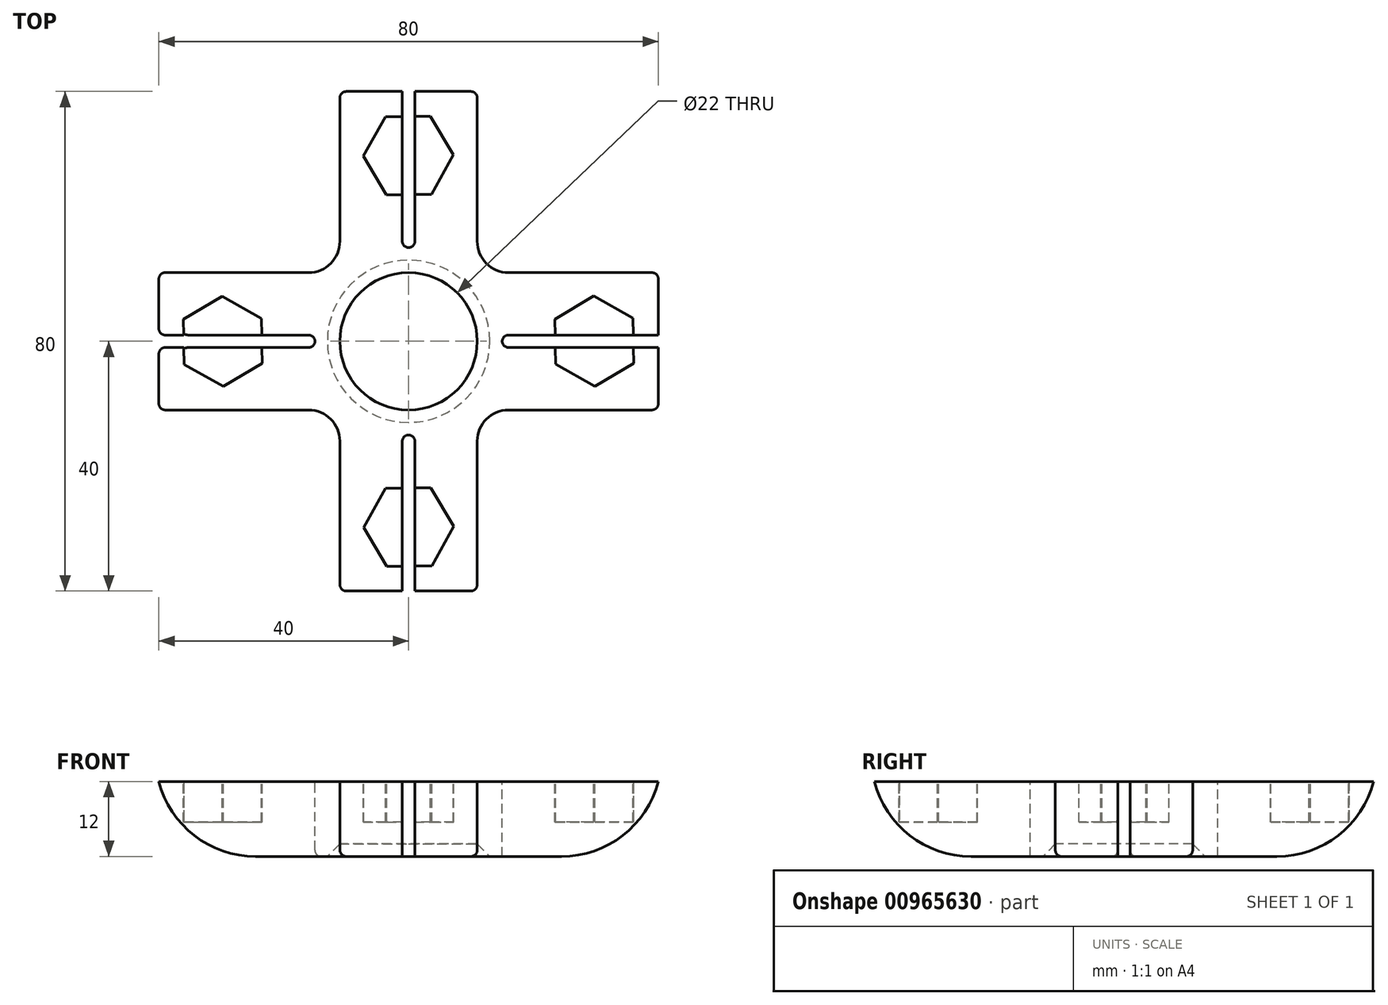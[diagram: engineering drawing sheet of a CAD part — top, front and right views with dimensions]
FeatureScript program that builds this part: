
annotation { "Feature Type Name" : "Feature", "Feature Type Description" : "" }
export const myFeature = defineFeature(function(context is Context, id is Id, definition is map)
    precondition{}
    {
        {
            var Q0;
            Q0=qCreatedBy(makeId("Front.planeOp"),FACE);
            var sketch = newSketch(context, id + "F0", { "sketchPlane" : qUnion([Q0])});
            skLineSegment(sketch, "E0.bottom", {"start": v(-11, 0) * mm, "end": v(11, 0) * mm});
            skLineSegment(sketch, "E0.top", {"start": v(-11, -40) * mm, "end": v(-1, -40) * mm});
            skLineSegment(sketch, "E0.left", {"start": v(-11, -16) * mm, "end": v(-11, -40) * mm});
            skLineSegment(sketch, "E0.right", {"start": v(11, -16) * mm, "end": v(11, -40) * mm});
            skLineSegment(sketch, "E1.1.0", {"start": v(40, -11) * mm, "end": v(40, -1) * mm});
            skLineSegment(sketch, "E1.1.2", {"start": v(16, 11) * mm, "end": v(40, 11) * mm});
            skLineSegment(sketch, "E1.2.0", {"start": v(11, 40) * mm, "end": v(1, 40) * mm});
            skLineSegment(sketch, "E1.3.0", {"start": v(-40, 11) * mm, "end": v(-40, 1) * mm});
            skLineSegment(sketch, "E1.3.1", {"start": v(-16, 11) * mm, "end": v(-40, 11) * mm});
            skLineSegment(sketch, "E1.3.2", {"start": v(-16, -11) * mm, "end": v(-40, -11) * mm});
            skPoint(sketch, "E1.center", {"position": v(0, 0) * mm});
            skPoint(sketch, "E2.orphan", {"position": v(0, 11) * mm});
            skLineSegment(sketch, "E3.trimOffspring", {"start": v(-11, 16) * mm, "end": v(-11, 40) * mm});
            skLineSegment(sketch, "E4.trimOffspring", {"start": v(11, 16) * mm, "end": v(11, 40) * mm});
            skLineSegment(sketch, "E5.trimOffspring", {"start": v(16, -11) * mm, "end": v(40, -11) * mm});
            skPoint(sketch, "E6.orphan", {"position": v(0, -11) * mm});
            skPoint(sketch, "E7.visualSharp", {"position": v(-40, 11) * mm});
            skLineSegment(sketch, "E7.filletArc", {"start": v(-40, 11) * mm, "end": v(-40, 11) * mm});
            skPoint(sketch, "E8.visualSharp", {"position": v(-40, -11) * mm});
            skLineSegment(sketch, "E8.filletArc", {"start": v(-40, -11) * mm, "end": v(-40, -11) * mm});
            skPoint(sketch, "E9.visualSharp", {"position": v(-11, -40) * mm});
            skLineSegment(sketch, "E9.filletArc", {"start": v(-11, -40) * mm, "end": v(-11, -40) * mm});
            skPoint(sketch, "E10.visualSharp", {"position": v(11, -40) * mm});
            skLineSegment(sketch, "E10.filletArc", {"start": v(11, -40) * mm, "end": v(11, -40) * mm});
            skPoint(sketch, "E11.visualSharp", {"position": v(40, -11) * mm});
            skLineSegment(sketch, "E11.filletArc", {"start": v(40, -11) * mm, "end": v(40, -11) * mm});
            skPoint(sketch, "E12.visualSharp", {"position": v(40, 11) * mm});
            skLineSegment(sketch, "E12.filletArc", {"start": v(40, 11) * mm, "end": v(40, 11) * mm});
            skPoint(sketch, "E13.visualSharp", {"position": v(11, 40) * mm});
            skLineSegment(sketch, "E13.filletArc", {"start": v(11, 40) * mm, "end": v(11, 40) * mm});
            skPoint(sketch, "E14.visualSharp", {"position": v(-11, 40) * mm});
            skLineSegment(sketch, "E14.filletArc", {"start": v(-11, 40) * mm, "end": v(-11, 40) * mm});
            skArc(sketch, "E15.filletArc", {"start": v(-16, 11) * mm, "mid": v(-12.46, 12.46) * mm, "end": v(-11, 16) * mm});
            skArc(sketch, "E16.filletArc", {"start": v(11, 16) * mm, "mid": v(12.46, 12.46) * mm, "end": v(16, 11) * mm});
            skArc(sketch, "E17.filletArc", {"start": v(16, -11) * mm, "mid": v(12.46, -12.46) * mm, "end": v(11, -16) * mm});
            skArc(sketch, "E18.filletArc", {"start": v(-11, -16) * mm, "mid": v(-12.46, -12.46) * mm, "end": v(-16, -11) * mm});
            skLineSegment(sketch, "E19.0", {"start": v(-1, 40) * mm, "end": v(-1, 16) * mm});
            skLineSegment(sketch, "E20.0", {"start": v(1, 40) * mm, "end": v(1, 16) * mm});
            skLineSegment(sketch, "E21", {"start": v(0, 11) * mm, "end": v(0, 11) * mm});
            skLineSegment(sketch, "E22.trimOffspring", {"start": v(-1, 40) * mm, "end": v(-11, 40) * mm});
            skLineSegment(sketch, "E23.1.0", {"start": v(-40, -1) * mm, "end": v(-16, -1) * mm});
            skPoint(sketch, "E23.1.1", {"position": v(-11, 0) * mm});
            skLineSegment(sketch, "E23.1.2", {"start": v(-40, 1) * mm, "end": v(-16, 1) * mm});
            skLineSegment(sketch, "E23.1.3", {"start": v(-11, 0) * mm, "end": v(-11, 0) * mm});
            skLineSegment(sketch, "E23.2.0", {"start": v(1, -40) * mm, "end": v(1, -16) * mm});
            skLineSegment(sketch, "E23.2.2", {"start": v(-1, -40) * mm, "end": v(-1, -16) * mm});
            skLineSegment(sketch, "E23.2.3", {"start": v(0, -11) * mm, "end": v(0, -11) * mm});
            skLineSegment(sketch, "E23.3.0", {"start": v(40, 1) * mm, "end": v(16, 1) * mm});
            skPoint(sketch, "E23.3.1", {"position": v(11, 0) * mm});
            skLineSegment(sketch, "E23.3.2", {"start": v(40, -1) * mm, "end": v(16, -1) * mm});
            skLineSegment(sketch, "E23.3.3", {"start": v(11, 0) * mm, "end": v(11, 0) * mm});
            skLineSegment(sketch, "E24.trimOffspring", {"start": v(40, 1) * mm, "end": v(40, 11) * mm});
            skLineSegment(sketch, "E25.trimOffspring", {"start": v(1, -40) * mm, "end": v(11, -40) * mm});
            skLineSegment(sketch, "E26.trimOffspring", {"start": v(-40, -1) * mm, "end": v(-40, -11) * mm});
            skPoint(sketch, "E27.visualSharp", {"position": v(-11, -1) * mm});
            skPoint(sketch, "E28.visualSharp", {"position": v(-11, 1) * mm});
            skArc(sketch, "E28.filletArc", {"start": v(-15, 0) * mm, "mid": v(-15.3, 0.7) * mm, "end": v(-16, 1) * mm});
            skArc(sketch, "E29.filletArc", {"start": v(-16, -1) * mm, "mid": v(-15.3, -0.7) * mm, "end": v(-15, 0) * mm});
            skPoint(sketch, "E30.visualSharp", {"position": v(1, 11) * mm});
            skArc(sketch, "E30.filletArc", {"start": v(0, 15) * mm, "mid": v(0.7, 15.3) * mm, "end": v(1, 16) * mm});
            skPoint(sketch, "E31.visualSharp", {"position": v(-1, 11) * mm});
            skArc(sketch, "E31.filletArc", {"start": v(-1, 16) * mm, "mid": v(-0.7, 15.3) * mm, "end": v(0, 15) * mm});
            skPoint(sketch, "E32.visualSharp", {"position": v(11, 1) * mm});
            skArc(sketch, "E32.filletArc", {"start": v(16, 1) * mm, "mid": v(15.3, 0.7) * mm, "end": v(15, 0) * mm});
            skPoint(sketch, "E33.visualSharp", {"position": v(11, -1) * mm});
            skArc(sketch, "E33.filletArc", {"start": v(15, 0) * mm, "mid": v(15.3, -0.7) * mm, "end": v(16, -1) * mm});
            skPoint(sketch, "E34.visualSharp", {"position": v(-1, -11) * mm});
            skArc(sketch, "E34.filletArc", {"start": v(0, -15) * mm, "mid": v(-0.7, -15.3) * mm, "end": v(-1, -16) * mm});
            skPoint(sketch, "E35.visualSharp", {"position": v(1, -11) * mm});
            skArc(sketch, "E35.filletArc", {"start": v(1, -16) * mm, "mid": v(0.7, -15.3) * mm, "end": v(0, -15) * mm});
            skSolve(sketch);
        }
        {
            var Q0;
            Q0=qCreatedBy(makeId("Front.planeOp"),FACE);
            var sketch = newSketch(context, id + "F1", { "sketchPlane" : qUnion([Q0])});
            skCircle(sketch, "E36.cCircle", {"center": v(-0.02, -29.75) * mm, "radius": 6.25 * mm, "construction": true});
            skLineSegment(sketch, "E36.0", {"start": v(3.5, -36.05) * mm, "end": v(-3.71, -35.95) * mm});
            skLineSegment(sketch, "E36.1", {"start": v(-3.71, -35.95) * mm, "end": v(-7.24, -29.65) * mm});
            skLineSegment(sketch, "E36.2", {"start": v(-7.24, -29.65) * mm, "end": v(-3.54, -23.45) * mm});
            skLineSegment(sketch, "E36.3", {"start": v(-3.54, -23.45) * mm, "end": v(3.67, -23.55) * mm});
            skLineSegment(sketch, "E36.4", {"start": v(3.67, -23.55) * mm, "end": v(7.2, -29.85) * mm});
            skLineSegment(sketch, "E36.5", {"start": v(7.2, -29.85) * mm, "end": v(3.5, -36.05) * mm});
            skPoint(sketch, "E36.0.midPoint", {"position": v(-0.1, -36) * mm});
            skCircle(sketch, "E37.1.0", {"center": v(29.75, -0.02) * mm, "radius": 6.25 * mm, "construction": true});
            skPoint(sketch, "E37.1.1", {"position": v(36, -0.1) * mm});
            skLineSegment(sketch, "E37.1.2", {"start": v(23.55, 3.67) * mm, "end": v(29.85, 7.2) * mm});
            skLineSegment(sketch, "E37.1.3", {"start": v(35.95, -3.71) * mm, "end": v(29.65, -7.24) * mm});
            skLineSegment(sketch, "E37.1.4", {"start": v(29.85, 7.2) * mm, "end": v(36.05, 3.5) * mm});
            skLineSegment(sketch, "E37.1.5", {"start": v(23.45, -3.54) * mm, "end": v(23.55, 3.67) * mm});
            skLineSegment(sketch, "E37.1.6", {"start": v(29.65, -7.24) * mm, "end": v(23.45, -3.54) * mm});
            skLineSegment(sketch, "E37.1.7", {"start": v(36.05, 3.5) * mm, "end": v(35.95, -3.71) * mm});
            skCircle(sketch, "E37.2.0", {"center": v(0.02, 29.75) * mm, "radius": 6.25 * mm, "construction": true});
            skPoint(sketch, "E37.2.1", {"position": v(0.1, 36) * mm});
            skLineSegment(sketch, "E37.2.2", {"start": v(-3.67, 23.55) * mm, "end": v(-7.2, 29.85) * mm});
            skLineSegment(sketch, "E37.2.3", {"start": v(3.71, 35.95) * mm, "end": v(7.24, 29.65) * mm});
            skLineSegment(sketch, "E37.2.4", {"start": v(-7.2, 29.85) * mm, "end": v(-3.5, 36.05) * mm});
            skLineSegment(sketch, "E37.2.5", {"start": v(3.54, 23.45) * mm, "end": v(-3.67, 23.55) * mm});
            skLineSegment(sketch, "E37.2.6", {"start": v(7.24, 29.65) * mm, "end": v(3.54, 23.45) * mm});
            skLineSegment(sketch, "E37.2.7", {"start": v(-3.5, 36.05) * mm, "end": v(3.71, 35.95) * mm});
            skCircle(sketch, "E37.3.0", {"center": v(-29.75, 0.02) * mm, "radius": 6.25 * mm, "construction": true});
            skPoint(sketch, "E37.3.1", {"position": v(-36, 0.1) * mm});
            skLineSegment(sketch, "E37.3.2", {"start": v(-23.55, -3.67) * mm, "end": v(-29.85, -7.2) * mm});
            skLineSegment(sketch, "E37.3.3", {"start": v(-35.95, 3.71) * mm, "end": v(-29.65, 7.24) * mm});
            skLineSegment(sketch, "E37.3.4", {"start": v(-29.85, -7.2) * mm, "end": v(-36.05, -3.5) * mm});
            skLineSegment(sketch, "E37.3.5", {"start": v(-23.45, 3.54) * mm, "end": v(-23.55, -3.67) * mm});
            skLineSegment(sketch, "E37.3.6", {"start": v(-29.65, 7.24) * mm, "end": v(-23.45, 3.54) * mm});
            skLineSegment(sketch, "E37.3.7", {"start": v(-36.05, -3.5) * mm, "end": v(-35.95, 3.71) * mm});
            skPoint(sketch, "E37.center", {"position": v(0, 0) * mm});
            skSolve(sketch);
        }
        {
            var Q0;
            Q0=qCreatedBy(makeId("Front.planeOp"),FACE);
            var sketch = newSketch(context, id + "F2", { "sketchPlane" : qUnion([Q0])});
            skCircle(sketch, "E38", {"center": v(0, 0) * mm, "radius": 11 * mm});
            skSolve(sketch);
        }
        {
            var Q0;
            Q0 = qSketchRegion(id + "F0", true);
            extrude(context, id + "F3", {"entities" : qUnion([Q0]), "depth" : 12 * mm, "offsetDistance" : 25 * mm});
        }
        {
            var Q0;
            Q0 = qSketchRegion(id + "F1", true);
            extrude(context, id + "F4", {"entities" : qUnion([Q0]), "depth" : 6.5 * mm, "offsetDistance" : 25 * mm});
        }
        {
            var Q0;
            Q0 = qSketchRegion(id + "F2", true);
            extrude(context, id + "F5", {"entities" : qUnion([Q0]), "depth" : 25 * mm, "offsetDistance" : 25 * mm});
        }
        {
            var Q0;
            Q0=makeQuery(id+"F5.opExtrude","SWEPT_BODY",BODY,{"disambiguationData":[OSD([sQuery(id+"F2.wireOp",EDGE,"E38")])]});
            var Q1;
            Q1=makeQuery(id+"F4.opExtrude","SWEPT_BODY",BODY,{"disambiguationData":[OSD([sQuery(id+"F1.wireOp",EDGE,"E37.1.2"),sQuery(id+"F1.wireOp",EDGE,"E37.1.3"),sQuery(id+"F1.wireOp",EDGE,"E37.1.4"),sQuery(id+"F1.wireOp",EDGE,"E37.1.5"),sQuery(id+"F1.wireOp",EDGE,"E37.1.6"),sQuery(id+"F1.wireOp",EDGE,"E37.1.7")])]});
            var Q2;
            Q2=makeQuery(id+"F4.opExtrude","SWEPT_BODY",BODY,{"disambiguationData":[OSD([sQuery(id+"F1.wireOp",EDGE,"E37.2.2"),sQuery(id+"F1.wireOp",EDGE,"E37.2.3"),sQuery(id+"F1.wireOp",EDGE,"E37.2.4"),sQuery(id+"F1.wireOp",EDGE,"E37.2.5"),sQuery(id+"F1.wireOp",EDGE,"E37.2.6"),sQuery(id+"F1.wireOp",EDGE,"E37.2.7")])]});
            var Q3;
            Q3=makeQuery(id+"F4.opExtrude","SWEPT_BODY",BODY,{"disambiguationData":[OSD([sQuery(id+"F1.wireOp",EDGE,"E37.3.2"),sQuery(id+"F1.wireOp",EDGE,"E37.3.3"),sQuery(id+"F1.wireOp",EDGE,"E37.3.4"),sQuery(id+"F1.wireOp",EDGE,"E37.3.5"),sQuery(id+"F1.wireOp",EDGE,"E37.3.6"),sQuery(id+"F1.wireOp",EDGE,"E37.3.7")])]});
            var Q4;
            Q4=makeQuery(id+"F4.opExtrude","SWEPT_BODY",BODY,{"disambiguationData":[OSD([sQuery(id+"F1.wireOp",EDGE,"E36.0"),sQuery(id+"F1.wireOp",EDGE,"E36.1"),sQuery(id+"F1.wireOp",EDGE,"E36.2"),sQuery(id+"F1.wireOp",EDGE,"E36.3"),sQuery(id+"F1.wireOp",EDGE,"E36.4"),sQuery(id+"F1.wireOp",EDGE,"E36.5")])]});
            var Q5;
            Q5=makeQuery(id+"F3.opExtrude","SWEPT_BODY",BODY,{"disambiguationData":[OSD([sQuery(id+"F0.wireOp",EDGE,"E0.top"),sQuery(id+"F0.wireOp",EDGE,"E0.left"),sQuery(id+"F0.wireOp",EDGE,"E0.right"),sQuery(id+"F0.wireOp",EDGE,"E1.1.0"),sQuery(id+"F0.wireOp",EDGE,"E1.1.2"),sQuery(id+"F0.wireOp",EDGE,"E1.2.0"),sQuery(id+"F0.wireOp",EDGE,"E1.3.0"),sQuery(id+"F0.wireOp",EDGE,"E1.3.1"),sQuery(id+"F0.wireOp",EDGE,"E1.3.2"),sQuery(id+"F0.wireOp",EDGE,"E3.trimOffspring"),sQuery(id+"F0.wireOp",EDGE,"E4.trimOffspring"),sQuery(id+"F0.wireOp",EDGE,"E5.trimOffspring"),sQuery(id+"F0.wireOp",EDGE,"E15.filletArc"),sQuery(id+"F0.wireOp",EDGE,"E16.filletArc"),sQuery(id+"F0.wireOp",EDGE,"E17.filletArc"),sQuery(id+"F0.wireOp",EDGE,"E18.filletArc"),sQuery(id+"F0.wireOp",EDGE,"E19.0"),sQuery(id+"F0.wireOp",EDGE,"E20.0"),sQuery(id+"F0.wireOp",EDGE,"E22.trimOffspring"),sQuery(id+"F0.wireOp",EDGE,"E23.1.0"),sQuery(id+"F0.wireOp",EDGE,"E23.1.2"),sQuery(id+"F0.wireOp",EDGE,"E23.2.0"),sQuery(id+"F0.wireOp",EDGE,"E23.2.2"),sQuery(id+"F0.wireOp",EDGE,"E23.3.0"),sQuery(id+"F0.wireOp",EDGE,"E23.3.2"),sQuery(id+"F0.wireOp",EDGE,"E24.trimOffspring"),sQuery(id+"F0.wireOp",EDGE,"E25.trimOffspring"),sQuery(id+"F0.wireOp",EDGE,"E26.trimOffspring"),sQuery(id+"F0.wireOp",EDGE,"E28.filletArc"),sQuery(id+"F0.wireOp",EDGE,"E29.filletArc"),sQuery(id+"F0.wireOp",EDGE,"E30.filletArc"),sQuery(id+"F0.wireOp",EDGE,"E31.filletArc"),sQuery(id+"F0.wireOp",EDGE,"E32.filletArc"),sQuery(id+"F0.wireOp",EDGE,"E33.filletArc"),sQuery(id+"F0.wireOp",EDGE,"E34.filletArc"),sQuery(id+"F0.wireOp",EDGE,"E35.filletArc")])]});
            booleanBodies(context, id + "F6", {"operationType" : BooleanOperationType.SUBTRACTION, "tools" : qUnion([Q0, Q1, Q2, Q3, Q4]), "targets" : qUnion([Q5])});
        }
        {
            var Q0;
            Q0=makeQuery(id+"F3.opExtrude","CAP_EDGE",EDGE,{"disambiguationData":[OSD([sQuery(id+"F0.wireOp",EDGE,"E22.trimOffspring")])],"isStart":false});
            var Q1;
            Q1=makeQuery(id+"F3.opExtrude","CAP_EDGE",EDGE,{"disambiguationData":[OSD([sQuery(id+"F0.wireOp",EDGE,"E1.2.0")])],"isStart":false});
            var Q2;
            Q2=makeQuery(id+"F3.opExtrude","CAP_EDGE",EDGE,{"disambiguationData":[OSD([sQuery(id+"F0.wireOp",EDGE,"E24.trimOffspring")])],"isStart":false});
            var Q3;
            Q3=makeQuery(id+"F3.opExtrude","CAP_EDGE",EDGE,{"disambiguationData":[OSD([sQuery(id+"F0.wireOp",EDGE,"E1.1.0")])],"isStart":false});
            var Q4;
            Q4=makeQuery(id+"F3.opExtrude","CAP_EDGE",EDGE,{"disambiguationData":[OSD([sQuery(id+"F0.wireOp",EDGE,"E25.trimOffspring")])],"isStart":false});
            var Q5;
            Q5=makeQuery(id+"F3.opExtrude","CAP_EDGE",EDGE,{"disambiguationData":[OSD([sQuery(id+"F0.wireOp",EDGE,"E0.top")])],"isStart":false});
            var Q6;
            Q6=makeQuery(id+"F3.opExtrude","CAP_EDGE",EDGE,{"disambiguationData":[OSD([sQuery(id+"F0.wireOp",EDGE,"E1.3.0")])],"isStart":false});
            var Q7;
            Q7=makeQuery(id+"F3.opExtrude","CAP_EDGE",EDGE,{"disambiguationData":[OSD([sQuery(id+"F0.wireOp",EDGE,"E26.trimOffspring")])],"isStart":false});
            fillet(context, id + "F7", {"entities" : qUnion([Q0, Q1, Q2, Q3, Q4, Q5, Q6, Q7]), "radius" : 16 * mm, "tangentPropagation" : true, "allowEdgeOverflow" : false});
        }
        {
            var Q0;
            Q0=makeQuery(id+"F6.opBoolean","COPY",EDGE,{"derivedFrom":makeQuery(id+"F5.opExtrude","CAP_EDGE",EDGE,{"disambiguationData":[OSD([sQuery(id+"F2.wireOp",EDGE,"E38")])],"isStart":true})});
            var Q1;
            Q1=makeQuery(id+"F6.opBoolean","INTERSECT",EDGE,{"derivedFrom":[makeQuery(id+"F3.opExtrude","CAP_FACE",FACE,{"disambiguationData":[OSD([sQuery(id+"F0.wireOp",EDGE,"E0.top"),sQuery(id+"F0.wireOp",EDGE,"E0.left"),sQuery(id+"F0.wireOp",EDGE,"E0.right"),sQuery(id+"F0.wireOp",EDGE,"E1.1.0"),sQuery(id+"F0.wireOp",EDGE,"E1.1.2"),sQuery(id+"F0.wireOp",EDGE,"E1.2.0"),sQuery(id+"F0.wireOp",EDGE,"E1.3.0"),sQuery(id+"F0.wireOp",EDGE,"E1.3.1"),sQuery(id+"F0.wireOp",EDGE,"E1.3.2"),sQuery(id+"F0.wireOp",EDGE,"E3.trimOffspring"),sQuery(id+"F0.wireOp",EDGE,"E4.trimOffspring"),sQuery(id+"F0.wireOp",EDGE,"E5.trimOffspring"),sQuery(id+"F0.wireOp",EDGE,"E15.filletArc"),sQuery(id+"F0.wireOp",EDGE,"E16.filletArc"),sQuery(id+"F0.wireOp",EDGE,"E17.filletArc"),sQuery(id+"F0.wireOp",EDGE,"E18.filletArc"),sQuery(id+"F0.wireOp",EDGE,"E19.0"),sQuery(id+"F0.wireOp",EDGE,"E20.0"),sQuery(id+"F0.wireOp",EDGE,"E22.trimOffspring"),sQuery(id+"F0.wireOp",EDGE,"E23.1.0"),sQuery(id+"F0.wireOp",EDGE,"E23.1.2"),sQuery(id+"F0.wireOp",EDGE,"E23.2.0"),sQuery(id+"F0.wireOp",EDGE,"E23.2.2"),sQuery(id+"F0.wireOp",EDGE,"E23.3.0"),sQuery(id+"F0.wireOp",EDGE,"E23.3.2"),sQuery(id+"F0.wireOp",EDGE,"E24.trimOffspring"),sQuery(id+"F0.wireOp",EDGE,"E25.trimOffspring"),sQuery(id+"F0.wireOp",EDGE,"E26.trimOffspring"),sQuery(id+"F0.wireOp",EDGE,"E28.filletArc"),sQuery(id+"F0.wireOp",EDGE,"E29.filletArc"),sQuery(id+"F0.wireOp",EDGE,"E30.filletArc"),sQuery(id+"F0.wireOp",EDGE,"E31.filletArc"),sQuery(id+"F0.wireOp",EDGE,"E32.filletArc"),sQuery(id+"F0.wireOp",EDGE,"E33.filletArc"),sQuery(id+"F0.wireOp",EDGE,"E34.filletArc"),sQuery(id+"F0.wireOp",EDGE,"E35.filletArc")])],"isStart":false}),makeQuery(id+"F5.opExtrude","SWEPT_FACE",FACE,{"disambiguationData":[OSD([sQuery(id+"F2.wireOp",EDGE,"E38")])]})]});
            chamfer(context, id + "F8", {"entities" : qUnion([Q0, Q1]), "width" : 2 * mm, "tangentPropagation" : true});
        }
        {
            var Q0;
            Q0=makeQuery(id+"F7.opFillet","BLEND_EDGE",EDGE,{"blendedFrom":[makeQuery(id+"F3.opExtrude","CAP_EDGE",EDGE,{"disambiguationData":[OSD([sQuery(id+"F0.wireOp",EDGE,"E1.3.0")])],"isStart":false}),makeQuery(id+"F3.opExtrude","SWEPT_FACE",FACE,{"disambiguationData":[OSD([sQuery(id+"F0.wireOp",EDGE,"E1.3.1")])]})],"blendedInto":[makeQuery(id+"F3.opExtrude","SWEPT_FACE",FACE,{"disambiguationData":[OSD([sQuery(id+"F0.wireOp",EDGE,"E1.3.1")])]})]});
            var Q1;
            Q1=makeQuery(id+"F7.opFillet","BLEND_EDGE",EDGE,{"blendedFrom":[makeQuery(id+"F3.opExtrude","CAP_EDGE",EDGE,{"disambiguationData":[OSD([sQuery(id+"F0.wireOp",EDGE,"E26.trimOffspring")])],"isStart":false}),makeQuery(id+"F3.opExtrude","SWEPT_FACE",FACE,{"disambiguationData":[OSD([sQuery(id+"F0.wireOp",EDGE,"E23.1.0")])]})],"blendedInto":[makeQuery(id+"F3.opExtrude","SWEPT_FACE",FACE,{"disambiguationData":[OSD([sQuery(id+"F0.wireOp",EDGE,"E23.1.0")])]})]});
            var Q2;
            Q2=makeQuery(id+"F7.opFillet","BLEND_EDGE",EDGE,{"blendedFrom":[makeQuery(id+"F3.opExtrude","CAP_EDGE",EDGE,{"disambiguationData":[OSD([sQuery(id+"F0.wireOp",EDGE,"E26.trimOffspring")])],"isStart":false}),makeQuery(id+"F3.opExtrude","SWEPT_FACE",FACE,{"disambiguationData":[OSD([sQuery(id+"F0.wireOp",EDGE,"E1.3.2")])]})],"blendedInto":[makeQuery(id+"F3.opExtrude","SWEPT_FACE",FACE,{"disambiguationData":[OSD([sQuery(id+"F0.wireOp",EDGE,"E1.3.2")])]})]});
            var Q3;
            Q3=makeQuery(id+"F7.opFillet","BLEND_EDGE",EDGE,{"blendedFrom":[makeQuery(id+"F3.opExtrude","CAP_EDGE",EDGE,{"disambiguationData":[OSD([sQuery(id+"F0.wireOp",EDGE,"E24.trimOffspring")])],"isStart":false}),makeQuery(id+"F3.opExtrude","SWEPT_FACE",FACE,{"disambiguationData":[OSD([sQuery(id+"F0.wireOp",EDGE,"E1.1.2")])]})],"blendedInto":[makeQuery(id+"F3.opExtrude","SWEPT_FACE",FACE,{"disambiguationData":[OSD([sQuery(id+"F0.wireOp",EDGE,"E1.1.2")])]})]});
            var Q4;
            Q4=makeQuery(id+"F7.opFillet","BLEND_EDGE",EDGE,{"blendedFrom":[makeQuery(id+"F3.opExtrude","CAP_EDGE",EDGE,{"disambiguationData":[OSD([sQuery(id+"F0.wireOp",EDGE,"E1.1.0")])],"isStart":false}),makeQuery(id+"F3.opExtrude","SWEPT_FACE",FACE,{"disambiguationData":[OSD([sQuery(id+"F0.wireOp",EDGE,"E5.trimOffspring")])]})],"blendedInto":[makeQuery(id+"F3.opExtrude","SWEPT_FACE",FACE,{"disambiguationData":[OSD([sQuery(id+"F0.wireOp",EDGE,"E5.trimOffspring")])]})]});
            fillet(context, id + "F9", {"entities" : qUnion([Q0, Q1, Q2, Q3, Q4]), "radius" : 1 * mm, "tangentPropagation" : true, "allowEdgeOverflow" : false});
        }
        {
            var Q0;
            Q0=makeQuery(id+"F3.opExtrude","SWEPT_BODY",BODY,{"disambiguationData":[OSD([sQuery(id+"F0.wireOp",EDGE,"E0.top"),sQuery(id+"F0.wireOp",EDGE,"E0.left"),sQuery(id+"F0.wireOp",EDGE,"E0.right"),sQuery(id+"F0.wireOp",EDGE,"E1.1.0"),sQuery(id+"F0.wireOp",EDGE,"E1.1.2"),sQuery(id+"F0.wireOp",EDGE,"E1.2.0"),sQuery(id+"F0.wireOp",EDGE,"E1.3.0"),sQuery(id+"F0.wireOp",EDGE,"E1.3.1"),sQuery(id+"F0.wireOp",EDGE,"E1.3.2"),sQuery(id+"F0.wireOp",EDGE,"E3.trimOffspring"),sQuery(id+"F0.wireOp",EDGE,"E4.trimOffspring"),sQuery(id+"F0.wireOp",EDGE,"E5.trimOffspring"),sQuery(id+"F0.wireOp",EDGE,"E15.filletArc"),sQuery(id+"F0.wireOp",EDGE,"E16.filletArc"),sQuery(id+"F0.wireOp",EDGE,"E17.filletArc"),sQuery(id+"F0.wireOp",EDGE,"E18.filletArc"),sQuery(id+"F0.wireOp",EDGE,"E19.0"),sQuery(id+"F0.wireOp",EDGE,"E20.0"),sQuery(id+"F0.wireOp",EDGE,"E22.trimOffspring"),sQuery(id+"F0.wireOp",EDGE,"E23.1.0"),sQuery(id+"F0.wireOp",EDGE,"E23.1.2"),sQuery(id+"F0.wireOp",EDGE,"E23.2.0"),sQuery(id+"F0.wireOp",EDGE,"E23.2.2"),sQuery(id+"F0.wireOp",EDGE,"E23.3.0"),sQuery(id+"F0.wireOp",EDGE,"E23.3.2"),sQuery(id+"F0.wireOp",EDGE,"E24.trimOffspring"),sQuery(id+"F0.wireOp",EDGE,"E25.trimOffspring"),sQuery(id+"F0.wireOp",EDGE,"E26.trimOffspring"),sQuery(id+"F0.wireOp",EDGE,"E28.filletArc"),sQuery(id+"F0.wireOp",EDGE,"E29.filletArc"),sQuery(id+"F0.wireOp",EDGE,"E30.filletArc"),sQuery(id+"F0.wireOp",EDGE,"E31.filletArc"),sQuery(id+"F0.wireOp",EDGE,"E32.filletArc"),sQuery(id+"F0.wireOp",EDGE,"E33.filletArc"),sQuery(id+"F0.wireOp",EDGE,"E34.filletArc"),sQuery(id+"F0.wireOp",EDGE,"E35.filletArc")])]});
            var Q1;
            Q1=sQuery(id+"F0.wireOp",EDGE,"E0.bottom");
            transform(context, id + "F10", {"entities" : qUnion([Q0]), "transformType" : TransformType.ROTATION, "transformAxis" : qUnion([Q1]), "angle" : 90 * degree, "makeCopy" : false});
        }
    });
